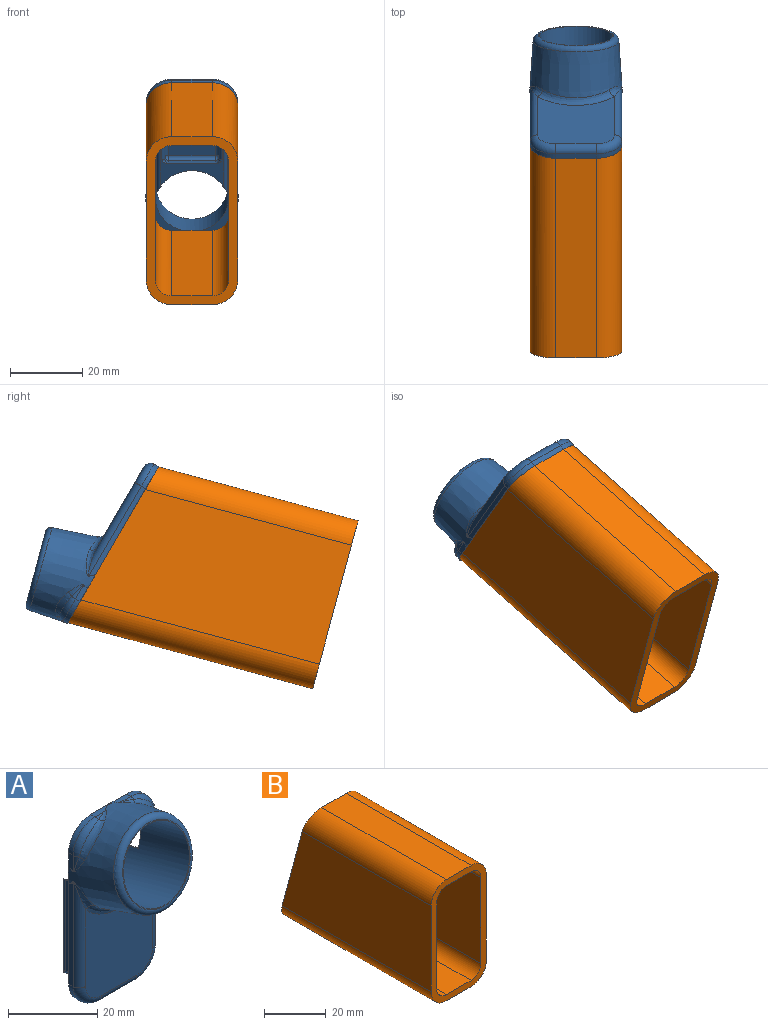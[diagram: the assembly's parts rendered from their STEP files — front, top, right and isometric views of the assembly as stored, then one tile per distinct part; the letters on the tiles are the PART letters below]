
ASSEMBLY  parts=2 mates=1
PART A: 69 faces, bbox 27x29x54.2 mm
  f0: plane 4.78x1.3mm, normal (0,0.26,0.97), area 1.6mm2, adj f20,f28,f36,f54
  f1: bspline ~2.16x2mm, area 2.3mm2, adj f20,f36,f53,f61
  f2: cone r=13.2mm half-angle=3.8deg, axis (0,0.97,-0.26), area 812mm2, adj f13,f14,f20,f21,f25,f26,f27,f38
  f3: plane 20.67x19.96mm, normal (0,-0.97,0.26), area 15.1mm2, adj f27,f28
  f4: cylinder r=2mm len=11.2mm, axis (-1,0,0), area 35.2mm2, adj f5,f6,f7,f9
  f5: torus R=5mm, axis (0,-1,0), area 31mm2, adj f4,f7,f8,f11
  f6: torus R=5mm, axis (0,-1,0), area 31mm2, adj f4,f7,f10,f12
  f7: plane 26.02x21.2mm, normal (0,-1,0), area 470.3mm2, adj f4,f5,f6,f11,f12,f45
  f8: cylinder r=7mm len=7mm, axis (0,1,0), area 15.4mm2, adj f5,f9,f14,f20
  f9: plane 11.2x1.4mm, normal (0,0,-1), area 15.7mm2, adj f4,f8,f10,f20
  f10: cylinder r=7mm len=7mm, axis (0,1,0), area 15.4mm2, adj f6,f9,f13,f20
  f11: cylinder r=2mm len=28.33mm, axis (0,0,-1), area 77.5mm2, adj f5,f7,f14,f44
  f12: cylinder r=2mm len=28.33mm, axis (0,0,1), area 77.5mm2, adj f6,f7,f13,f46
  f13: plane 28.49x1.56mm, normal (-1,0,0), area 39.1mm2, adj f2,f10,f12,f20,f46
  f14: plane 28.49x1.56mm, normal (1,0,0), area 39.1mm2, adj f2,f8,f11,f20,f44
  f15: cylinder r=7mm len=7mm, axis (0,1,0), area 15.4mm2, adj f18,f20,f21,f25
  f16: cylinder r=7mm len=7mm, axis (0,1,0), area 15.4mm2, adj f20,f23,f25,f26
  f17: cylinder r=2mm len=4.21mm, axis (0,0,1), area 3mm2, adj f18,f21,f39
  f18: torus R=5mm, axis (0,-1,0), area 18.6mm2, adj f15,f17,f19,f40
  f19: cylinder r=2mm len=2.78mm, axis (1,0,0), area 1.4mm2, adj f18,f25,f38
  f20: plane 50.01x25.58mm, normal (0,1,0), area 670.7mm2, adj f0,f1,f2,f8,f9,f10,f13,f14
  f21: plane 4.33x1.49mm, normal (-1,0,0), area 5.8mm2, adj f2,f15,f17,f20,f39
  f22: cylinder r=2mm len=4.21mm, axis (0,0,-1), area 3mm2, adj f23,f26,f41
  f23: torus R=5mm, axis (0,-1,0), area 18.6mm2, adj f16,f22,f24,f42
  f24: cylinder r=2mm len=2.78mm, axis (1,0,0), area 1.4mm2, adj f23,f25,f43
  f25: plane 11.39x1.59mm, normal (0,0,1), area 11.7mm2, adj f2,f15,f16,f19,f20,f24,f38,f43
  f26: plane 4.33x1.49mm, normal (1,0,0), area 5.8mm2, adj f2,f16,f20,f22,f41
  f27: torus R=10.34mm, axis (0,-0.97,0.26), area 159.7mm2, adj f2,f3
  f28: cylinder r=10.1mm len=28.09mm, axis (0,-0.97,0.26), area 1119.6mm2, adj f0,f3,f20,f29,f37,f48,f54
  f29: plane 4.78x1.3mm, normal (0,0.26,0.97), area 1.6mm2, adj f20,f28,f30,f48
  f30: plane 27.26x4.34mm, normal (-1,0,0), area 100.2mm2, adj f20,f29,f47,f48,f68
  f31: plane 3.74x1.01mm, normal (0,-0.26,-0.97), area 1.1mm2, adj f37,f47,f49,f67
  f32: plane 15.83x3mm, normal (1,0,0), area 45.1mm2, adj f49,f50,f63,f65
  f33: plane 13.23x3.74mm, normal (0,-0.26,-0.97), area 50.2mm2, adj f37,f55,f56,f57,f62,f63
  f34: plane 15.83x3mm, normal (-1,0,0), area 45.1mm2, adj f51,f52,f57,f59
  f35: plane 3.74x1.01mm, normal (0,-0.26,-0.97), area 1.1mm2, adj f37,f51,f53,f61
  f36: plane 27.26x4.34mm, normal (1,0,0), area 100.2mm2, adj f0,f1,f20,f53,f54
  f37: plane 25.11x18.13mm, normal (0,1,0), area 75.5mm2, adj f28,f31,f33,f35,f48,f50,f52,f54
  f38: bspline ~3.77x2.83mm, area 3.3mm2, adj f2,f19,f25,f40
  f39: bspline ~5.79x3.77mm, area 4.2mm2, adj f2,f17,f21,f40
  f40: bspline ~8.05x7.96mm, area 20.4mm2, adj f2,f18,f38,f39
  f41: bspline ~5.79x3.77mm, area 4.2mm2, adj f2,f22,f26,f42
  f42: bspline ~8.05x7.96mm, area 20.4mm2, adj f2,f23,f41,f43
  f43: bspline ~3.77x2.83mm, area 3.3mm2, adj f2,f24,f25,f42
  f44: bspline ~8.48x4.31mm, area 12mm2, adj f2,f11,f14,f45
  f45: bspline ~21.2x6.1mm, area 56.2mm2, adj f2,f7,f44,f46
  f46: bspline ~8.48x4.31mm, area 12mm2, adj f2,f12,f13,f45
  f47: cylinder r=1mm len=4.52mm, axis (0,-0.97,0.26), area 5.5mm2, adj f30,f31,f48,f68
  f48: cylinder r=1mm len=26.16mm, axis (0,0,-1), area 39.3mm2, adj f28,f29,f30,f37,f47
  f49: cylinder r=1mm len=4.52mm, axis (0,-0.97,0.26), area 5.5mm2, adj f31,f32,f50,f66
  f50: cylinder r=1mm len=16.32mm, axis (0,0,1), area 24.2mm2, adj f32,f37,f49,f62
  f51: cylinder r=1mm len=4.52mm, axis (0,0.97,-0.26), area 5.5mm2, adj f34,f35,f52,f60
  f52: cylinder r=1mm len=16.32mm, axis (0,0,-1), area 24.2mm2, adj f34,f37,f51,f56
  f53: cylinder r=1mm len=4.52mm, axis (0,0.97,-0.26), area 5.5mm2, adj f1,f35,f36,f54
  f54: cylinder r=1mm len=26.16mm, axis (0,0,1), area 39.3mm2, adj f0,f28,f36,f37,f53
  f55: cylinder r=1mm len=12.95mm, axis (-1,0,0), area 23.8mm2, adj f20,f33,f58,f64
  f56: bspline ~2.26x2mm, area 2.1mm2, adj f33,f37,f52,f57
  f57: cylinder r=1mm len=3.26mm, axis (0,-0.97,0.26), area 4.9mm2, adj f33,f34,f56,f58
  f58: sphere r=1mm, area 1.3mm2, adj f55,f57,f59
  f59: cylinder r=1mm len=15.02mm, axis (0,0,1), area 23.6mm2, adj f20,f34,f58,f60
  f60: bspline ~2.16x2mm, area 3.7mm2, adj f20,f51,f59,f61
  f61: cylinder r=1mm len=1.26mm, axis (-1,0,0), area 0.5mm2, adj f1,f20,f35,f60
  f62: bspline ~2.26x2mm, area 2.1mm2, adj f33,f37,f50,f63
  f63: cylinder r=1mm len=3.26mm, axis (0,0.97,-0.26), area 4.9mm2, adj f32,f33,f62,f64
  f64: sphere r=1mm, area 2.4mm2, adj f55,f63,f65
  f65: cylinder r=1mm len=15.02mm, axis (0,0,-1), area 23.6mm2, adj f20,f32,f64,f66
  f66: bspline ~2.35x2.16mm, area 3.7mm2, adj f20,f49,f65,f67
  f67: cylinder r=1mm len=1.26mm, axis (-1,0,0), area 0.5mm2, adj f20,f31,f66,f68
  f68: bspline ~2.16x2.09mm, area 2.3mm2, adj f20,f30,f47,f67
PART B: 18 faces, bbox 25.2x70x48 mm
  f0: plane 68.11x34mm, normal (1,0,0), area 2159.8mm2, adj f1,f15,f16,f17
  f1: cylinder r=7mm len=58.94mm, axis (0,1,0), area 634.8mm2, adj f0,f2,f16,f17
  f2: plane 57.05x11.2mm, normal (0,0,1), area 638.9mm2, adj f1,f3,f16,f17
  f3: cylinder r=7mm len=58.94mm, axis (0,1,0), area 634.8mm2, adj f2,f4,f16,f17
  f4: plane 68.11x34mm, normal (-1,0,0), area 2159.8mm2, adj f3,f5,f16,f17
  f5: cylinder r=7mm len=70mm, axis (0,1,0), area 762.1mm2, adj f4,f6,f16,f17
  f6: plane 70x11.2mm, normal (0,0,-1), area 784mm2, adj f5,f15,f16,f17
  f7: cylinder r=4.5mm len=69.33mm, axis (0,1,0), area 486.9mm2, adj f8,f14,f16,f17
  f8: plane 69.33x11.2mm, normal (0,0,1), area 776.4mm2, adj f7,f9,f16,f17
  f9: cylinder r=4.5mm len=69.33mm, axis (0,1,0), area 486.9mm2, adj f8,f10,f16,f17
  f10: plane 68.11x34mm, normal (1,0,0), area 2159.8mm2, adj f9,f11,f16,f17
  f11: cylinder r=4.5mm len=58.94mm, axis (0,1,0), area 411.1mm2, adj f10,f12,f16,f17
  f12: plane 57.72x11.2mm, normal (0,0,-1), area 646.5mm2, adj f11,f13,f16,f17
  f13: cylinder r=4.5mm len=58.94mm, axis (0,1,0), area 411.1mm2, adj f12,f14,f16,f17
  f14: plane 68.11x34mm, normal (-1,0,0), area 2159.8mm2, adj f7,f13,f16,f17
  f15: cylinder r=7mm len=70mm, axis (0,1,0), area 762.1mm2, adj f0,f6,f16,f17
  f16: plane 48x25.2mm, normal (0,-1,0), area 316.3mm2, adj f0,f1,f2,f3,f4,f5,f6,f7
  f17: plane 48x25.2mm, normal (0,0.97,0.26), area 327.6mm2, adj f0,f1,f2,f3,f4,f5,f6,f7
PLACE A rot(axis=(-1,0,0),149.8deg) t=(-0.02,22.75,-3.07)mm
PLACE B rot(axis=(1,0,0),15.1deg) t=(-0.02,28.93,-1.26)mm
MATE parallel B.f17 <-> A.f20  axis (0,0.86,0.5) through (-0.02,10.18,18.53)mm
